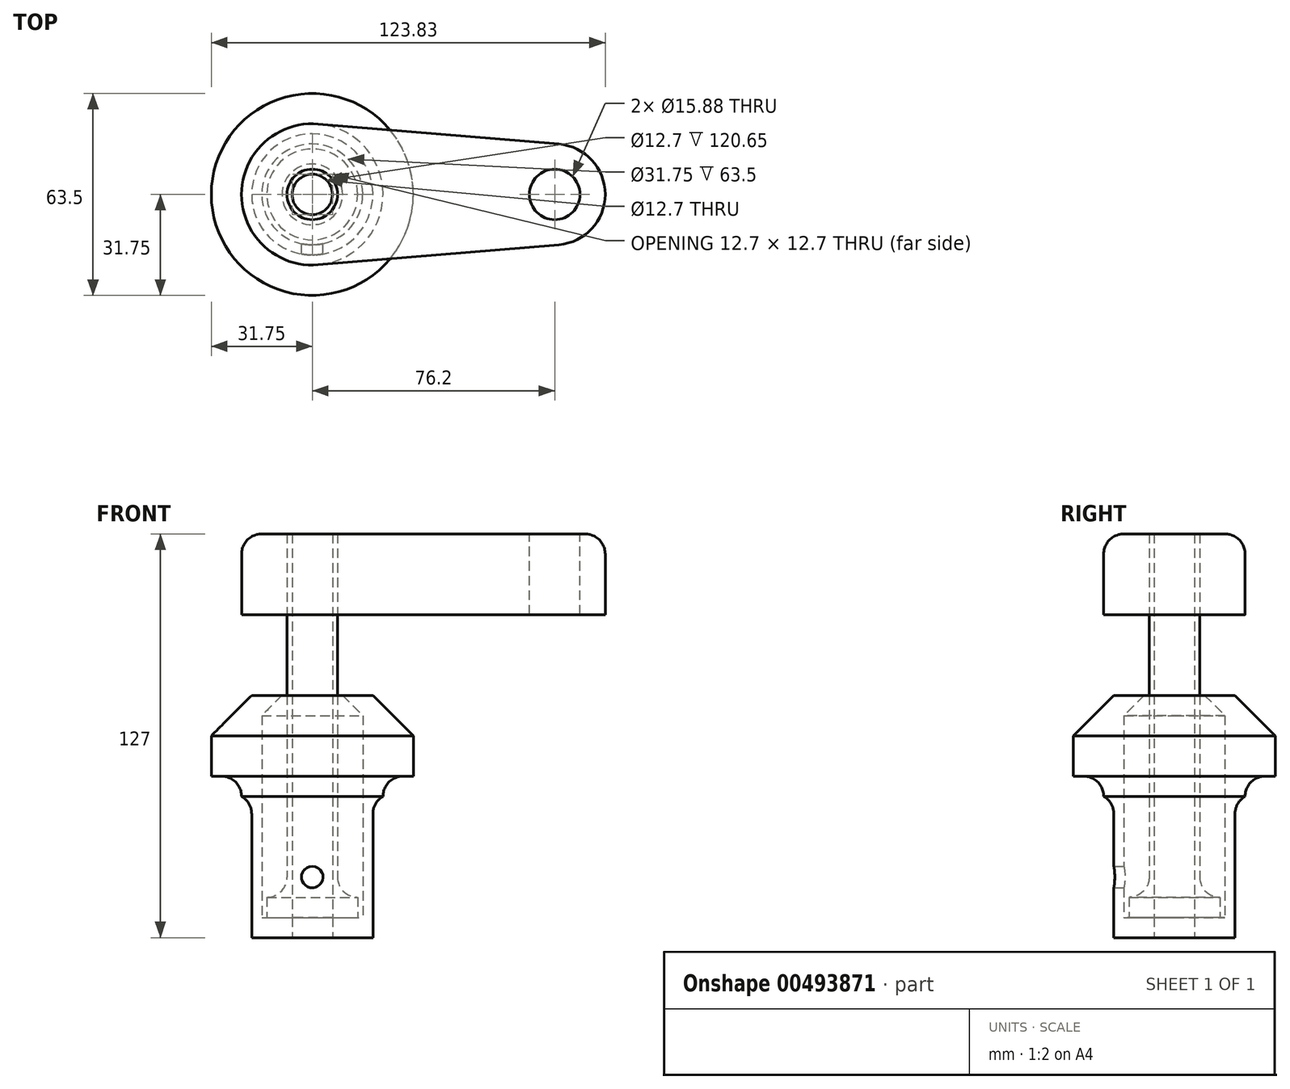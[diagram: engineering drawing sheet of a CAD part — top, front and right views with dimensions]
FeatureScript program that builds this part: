
annotation { "Feature Type Name" : "Feature", "Feature Type Description" : "" }
export const myFeature = defineFeature(function(context is Context, id is Id, definition is map)
    precondition{}
    {
        {
            var Q0;
            Q0=qCreatedBy(makeId("Front.planeOp"),FACE);
            var sketch = newSketch(context, id + "F0", { "sketchPlane" : qUnion([Q0])});
            skLineSegment(sketch, "E0", {"start": v(0, 0) * mm, "end": v(0, 76.2) * mm});
            skLineSegment(sketch, "E1", {"start": v(0, 76.2) * mm, "end": v(19.05, 76.2) * mm});
            skLineSegment(sketch, "E2", {"start": v(19.05, 76.2) * mm, "end": v(31.75, 63.5) * mm});
            skLineSegment(sketch, "E3", {"start": v(31.75, 63.5) * mm, "end": v(31.75, 50.8) * mm});
            skLineSegment(sketch, "E4", {"start": v(31.75, 50.8) * mm, "end": v(22.23, 50.8) * mm});
            skLineSegment(sketch, "E5", {"start": v(22.23, 50.8) * mm, "end": v(22.23, 44.45) * mm});
            skLineSegment(sketch, "E6", {"start": v(22.23, 44.45) * mm, "end": v(19.05, 44.45) * mm});
            skLineSegment(sketch, "E7", {"start": v(19.05, 44.45) * mm, "end": v(19.05, 0) * mm});
            skLineSegment(sketch, "E8", {"start": v(19.05, 0) * mm, "end": v(0, 0) * mm});
            skLineSegment(sketch, "E9", {"start": v(9.53, 76.2) * mm, "end": v(15.88, 69.85) * mm});
            skLineSegment(sketch, "E10", {"start": v(15.88, 69.85) * mm, "end": v(15.88, 6.35) * mm});
            skLineSegment(sketch, "E11", {"start": v(15.88, 6.35) * mm, "end": v(0, 6.35) * mm});
            skLineSegment(sketch, "E12", {"start": v(0, 76.2) * mm, "end": v(0, 87.5) * mm, "construction": true});
            skLineSegment(sketch, "E13", {"start": v(0, 76.2) * mm, "end": v(0, 127) * mm});
            skLineSegment(sketch, "E14", {"start": v(0, 127) * mm, "end": v(7.94, 127) * mm});
            skLineSegment(sketch, "E15", {"start": v(7.94, 127) * mm, "end": v(7.94, 12.7) * mm});
            skLineSegment(sketch, "E16", {"start": v(7.94, 12.7) * mm, "end": v(14.29, 12.7) * mm});
            skLineSegment(sketch, "E17", {"start": v(14.29, 12.7) * mm, "end": v(14.29, 6.35) * mm});
            skSolve(sketch);
        }
        {
            var Q0;
            {var subQ4=sQuery(id+"F0.wireOp",EDGE,"E2");Q0=makeQuery(id+"F0.imprint","IMPRINT",FACE,{"disambiguationData":[TD([[makeQuery(id+"F0.imprint","IMPRINT",EDGE,{"derivedFrom":subQ4}),-1.0]])]});}
            var Q1;
            Q1=sQuery(id+"F0.wireOp",EDGE,"E0");
            revolve(context, id + "F1", {"entities" : qUnion([Q0]), "axis" : qUnion([Q1]), "revolveType" : RevolveType.FULL});
        }
        {
            var Q0;
            {var subQ0=sQuery(id+"F0.wireOp",EDGE,"E13");Q0=makeQuery(id+"F0.imprint","IMPRINT",FACE,{"disambiguationData":[TD([[makeQuery(id+"F0.imprint","IMPRINT",EDGE,{"derivedFrom":subQ0}),-1.0]])]});}
            var Q1;
            {var subQ0=sQuery(id+"F0.wireOp",EDGE,"E16");Q1=makeQuery(id+"F0.imprint","IMPRINT",FACE,{"disambiguationData":[TD([[makeQuery(id+"F0.imprint","IMPRINT",EDGE,{"derivedFrom":subQ0}),-1.0]])]});}
            var Q2;
            Q2=sQuery(id+"F0.wireOp",EDGE,"E13");
            revolve(context, id + "F2", {"entities" : qUnion([Q0, Q1]), "axis" : qUnion([Q2]), "revolveType" : RevolveType.FULL});
        }
        {
            var Q0;
            Q0=makeQuery(id+"F2.opRevolve","SWEPT_FACE",FACE,{"disambiguationData":[OSD([sQuery(id+"F0.wireOp",EDGE,"E14")])]});
            var sketch = newSketch(context, id + "F3", { "sketchPlane" : qUnion([Q0])});
            skCircle(sketch, "E18.0", {"center": v(0, 0) * mm, "radius": 7.94 * mm});
            skCircle(sketch, "E19", {"center": v(0, 0) * mm, "radius": 22.23 * mm});
            skCircle(sketch, "E20", {"center": v(76.2, 0) * mm, "radius": 15.88 * mm});
            skCircle(sketch, "E21", {"center": v(76.2, 0) * mm, "radius": 7.94 * mm});
            skLineSegment(sketch, "E22", {"start": v(77.52, -15.82) * mm, "end": v(1.85, -22.15) * mm});
            skLineSegment(sketch, "E23", {"start": v(1.85, 22.15) * mm, "end": v(77.52, 15.82) * mm});
            skSolve(sketch);
        }
        {
            var Q0;
            Q0 = qSketchRegion(id + "F3", true);
            var Q1;
            Q1=makeQuery(id+"F1.opRevolve","SWEPT_FACE",FACE,{"disambiguationData":[OSD([sQuery(id+"F0.wireOp",EDGE,"E1")])]});
            extrude(context, id + "F4", {"entities" : qUnion([Q0]), "oppositeDirection" : true, "endBoundEntityFace" : qUnion([Q1]), "depth" : 25.4 * mm});
        }
        {
            var Q0;
            Q0=qCreatedBy(makeId("Front.planeOp"),FACE);
            var sketch = newSketch(context, id + "F5", { "sketchPlane" : qUnion([Q0])});
            skPoint(sketch, "E24", {"position": v(0, 19.05) * mm});
            skSolve(sketch);
        }
        {
            var Q0;
            Q0=sQuery(id+"F5.wireOp",VERTEX,"E24");
            var Q1;
            Q1=makeQuery(id+"F1.opRevolve","SWEPT_BODY",BODY,{"disambiguationData":[OSD([sQuery(id+"F0.wireOp",EDGE,"E0"),sQuery(id+"F0.wireOp",EDGE,"E1"),sQuery(id+"F0.wireOp",EDGE,"E2"),sQuery(id+"F0.wireOp",EDGE,"E3"),sQuery(id+"F0.wireOp",EDGE,"E4"),sQuery(id+"F0.wireOp",EDGE,"E5"),sQuery(id+"F0.wireOp",EDGE,"E6"),sQuery(id+"F0.wireOp",EDGE,"E7"),sQuery(id+"F0.wireOp",EDGE,"E8"),sQuery(id+"F0.wireOp",EDGE,"E9"),sQuery(id+"F0.wireOp",EDGE,"E10"),sQuery(id+"F0.wireOp",EDGE,"E11")])]});
            hole(context, id + "F6", {"style" : HoleStyle.SIMPLE, "endStyle" : HoleEndStyle.THROUGH, "oppositeDirection" : true, "standardTappedOrClearance" : lookupTablePath({ "standard" : "ANSI", "fit" : "Normal (ASME)", "size" : "1/4", "type" : "Clearance" }), "standardBlindInLast" : lookupTablePath({ "fit" : "Free", "standard" : "ANSI", "size" : "1/4", "type" : "Clearance" }), "holeDiameter" : 6.76 * mm, "tappedDepth" : 14.3 * mm, "tapClearance" : 3, "locations" : qUnion([Q0]), "scope" : qUnion([Q1])});
        }
        {
            var Q0;
            Q0=makeQuery(id+"F4.opExtrude","CAP_EDGE",EDGE,{"disambiguationData":[OSD([sQuery(id+"F3.wireOp",EDGE,"E22")])],"isStart":true});
            var Q1;
            Q1=makeQuery(id+"F1.opRevolve","SWEPT_EDGE",EDGE,{"disambiguationData":[OSD([sQuery(id+"F0.wireOp",EDGE,"E6"),sQuery(id+"F0.wireOp",EDGE,"E7")])]});
            var Q2;
            Q2=makeQuery(id+"F1.opRevolve","SWEPT_EDGE",EDGE,{"disambiguationData":[OSD([sQuery(id+"F0.wireOp",EDGE,"E4"),sQuery(id+"F0.wireOp",EDGE,"E5")])]});
            var Q3;
            Q3=makeQuery(id+"F2.opRevolve","SWEPT_EDGE",EDGE,{"disambiguationData":[OSD([sQuery(id+"F0.wireOp",EDGE,"E15"),sQuery(id+"F0.wireOp",EDGE,"E16")])]});
            fillet(context, id + "F7", {"entities" : qUnion([Q0, Q1, Q2, Q3]), "radius" : 6.35 * mm, "tangentPropagation" : true, "allowEdgeOverflow" : false});
        }
        {
            var Q0;
            Q0=makeQuery(id+"F1.opRevolve","SWEPT_FACE",FACE,{"disambiguationData":[OSD([sQuery(id+"F0.wireOp",EDGE,"E8")])]});
            var sketch = newSketch(context, id + "F8", { "sketchPlane" : qUnion([Q0])});
            skCircle(sketch, "E25", {"center": v(0, 0) * mm, "radius": 6.35 * mm});
            skSolve(sketch);
        }
        {
            var Q0;
            Q0 = qSketchRegion(id + "F8", true);
            extrude(context, id + "F9", {"entities" : qUnion([Q0]), "operationType" : NewBodyOperationType.REMOVE, "endBound" : BoundingType.THROUGH_ALL, "oppositeDirection" : true, "depth" : 25.4 * mm, "offsetDistance" : 25.4 * mm});
        }
    });
